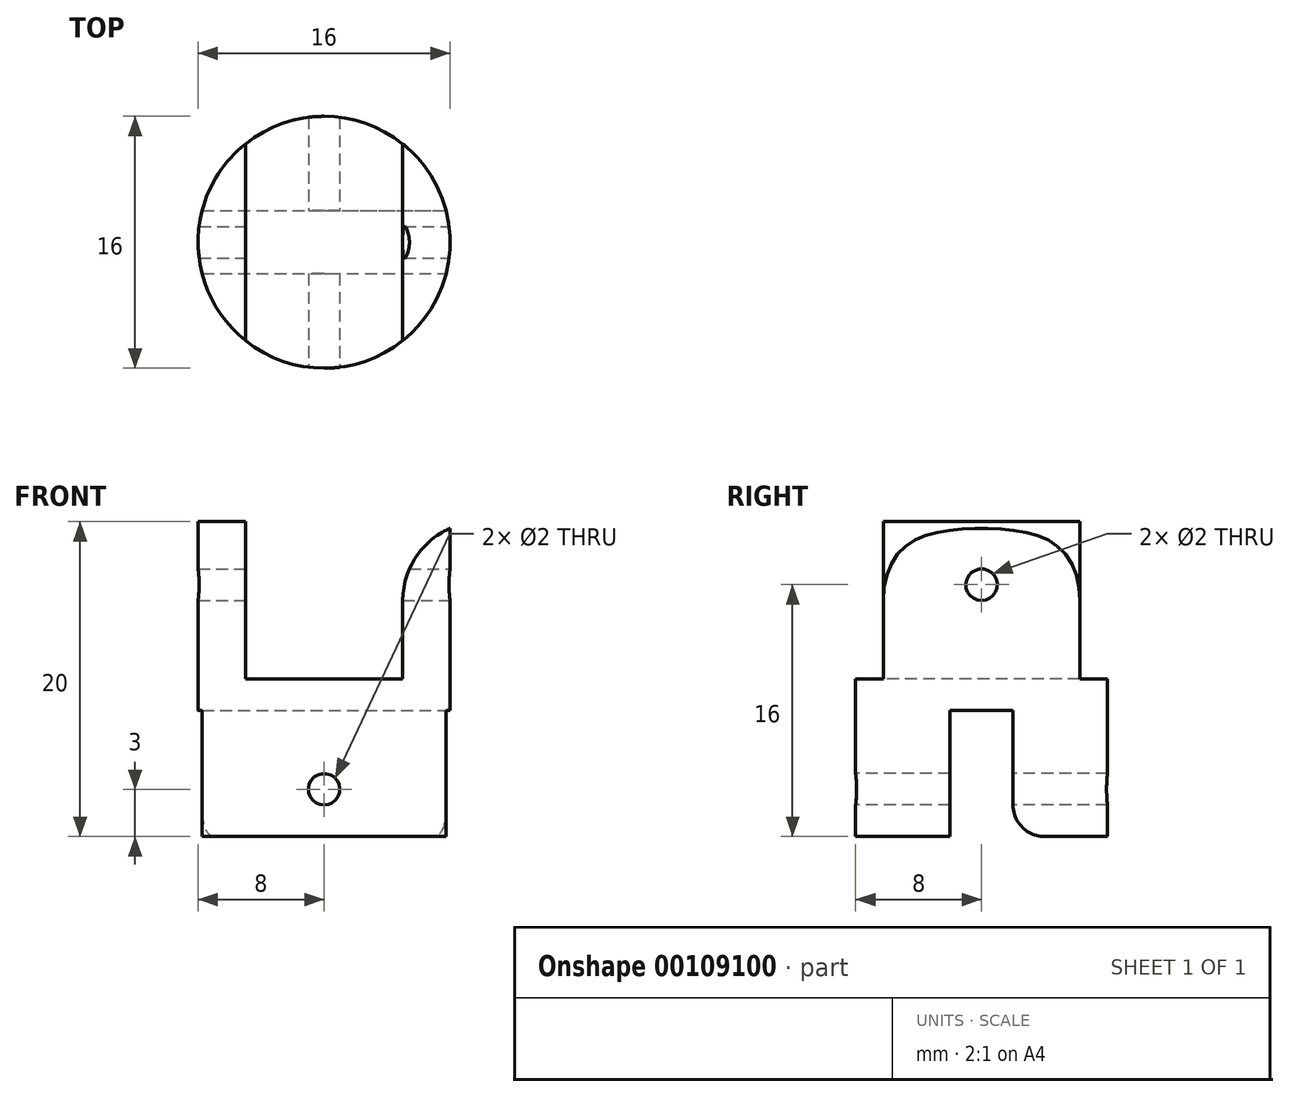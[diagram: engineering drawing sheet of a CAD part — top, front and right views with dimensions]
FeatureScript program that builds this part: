
annotation { "Feature Type Name" : "Feature", "Feature Type Description" : "" }
export const myFeature = defineFeature(function(context is Context, id is Id, definition is map)
    precondition{}
    {
        {
            var Q0;
            Q0=qCreatedBy(makeId("Top.planeOp"),FACE);
            var sketch = newSketch(context, id + "F0", { "sketchPlane" : qUnion([Q0])});
            skCircle(sketch, "E0", {"center": v(0, 0) * mm, "radius": 8 * mm});
            skSolve(sketch);
        }
        {
            var Q0;
            Q0 = qSketchRegion(id + "F0", true);
            extrude(context, id + "F1", {"entities" : qUnion([Q0]), "depth" : 20 * mm});
        }
        {
            var Q0;
            Q0=makeQuery(id+"F1.opExtrude","CAP_FACE",FACE,{"disambiguationData":[OSD([sQuery(id+"F0.wireOp",EDGE,"E0")])],"isStart":false});
            var sketch = newSketch(context, id + "F2", { "sketchPlane" : qUnion([Q0])});
            skLineSegment(sketch, "E1.bottom", {"start": v(-5, 8) * mm, "end": v(5, 8) * mm});
            skLineSegment(sketch, "E1.top", {"start": v(-5, -8) * mm, "end": v(5, -8) * mm});
            skLineSegment(sketch, "E1.left", {"start": v(-5, 8) * mm, "end": v(-5, -8) * mm});
            skLineSegment(sketch, "E1.right", {"start": v(5, 8) * mm, "end": v(5, -8) * mm});
            skPoint(sketch, "E1.middle", {"position": v(0, 0) * mm});
            skSolve(sketch);
        }
        {
            var Q0;
            Q0 = qSketchRegion(id + "F2", true);
            extrude(context, id + "F3", {"entities" : qUnion([Q0]), "operationType" : NewBodyOperationType.REMOVE, "oppositeDirection" : true, "depth" : 10 * mm});
        }
        {
            var Q0;
            Q0=makeQuery(id+"F1.opExtrude","CAP_FACE",FACE,{"disambiguationData":[OSD([sQuery(id+"F0.wireOp",EDGE,"E0")])],"isStart":true});
            var sketch = newSketch(context, id + "F4", { "sketchPlane" : qUnion([Q0])});
            skLineSegment(sketch, "E2.bottom", {"start": v(-8, -2) * mm, "end": v(8, -2) * mm});
            skLineSegment(sketch, "E2.top", {"start": v(-8, 2) * mm, "end": v(8, 2) * mm});
            skLineSegment(sketch, "E2.left", {"start": v(-8, -2) * mm, "end": v(-8, 2) * mm});
            skLineSegment(sketch, "E2.right", {"start": v(8, -2) * mm, "end": v(8, 2) * mm});
            skPoint(sketch, "E2.middle", {"position": v(0, 0) * mm});
            skSolve(sketch);
        }
        {
            var Q0;
            Q0 = qSketchRegion(id + "F4", true);
            extrude(context, id + "F5", {"entities" : qUnion([Q0]), "operationType" : NewBodyOperationType.REMOVE, "oppositeDirection" : true, "depth" : 8 * mm});
        }
        {
            var Q0;
            Q0=qCreatedBy(makeId("Right.planeOp"),FACE);
            var sketch = newSketch(context, id + "F6", { "sketchPlane" : qUnion([Q0])});
            skCircle(sketch, "E3", {"center": v(0, 16) * mm, "radius": 1 * mm});
            skSolve(sketch);
        }
        {
            var Q0;
            Q0 = qSketchRegion(id + "F6", true);
            extrude(context, id + "F7", {"entities" : qUnion([Q0]), "operationType" : NewBodyOperationType.REMOVE, "endBound" : BoundingType.SYMMETRIC, "oppositeDirection" : true, "depth" : 16 * mm});
        }
        {
            var Q0;
            Q0=qCreatedBy(makeId("Front.planeOp"),FACE);
            var sketch = newSketch(context, id + "F8", { "sketchPlane" : qUnion([Q0])});
            skCircle(sketch, "E4", {"center": v(0, 3) * mm, "radius": 1 * mm});
            skSolve(sketch);
        }
        {
            var Q0;
            Q0 = qSketchRegion(id + "F8", true);
            extrude(context, id + "F9", {"entities" : qUnion([Q0]), "operationType" : NewBodyOperationType.REMOVE, "endBound" : BoundingType.SYMMETRIC, "oppositeDirection" : true, "depth" : 16 * mm});
        }
        {
            var Q0;
            Q0=makeQuery(id+"F3.boolean.opBoolean","COPY",EDGE,{"derivedFrom":makeQuery(id+"F3.opExtrude","CAP_EDGE",EDGE,{"disambiguationData":[OSD([sQuery(id+"F2.wireOp",EDGE,"E1.left")])],"isStart":true})});
            var Q1;
            Q1=makeQuery(id+"F3.boolean.opBoolean","COPY",EDGE,{"derivedFrom":makeQuery(id+"F3.opExtrude","CAP_EDGE",EDGE,{"disambiguationData":[OSD([sQuery(id+"F2.wireOp",EDGE,"E1.right")])],"isStart":true})});
            fillet(context, id + "F10", {"entities" : qUnion([Q0, Q1]), "radius" : 5 * mm, "tangentPropagation" : true, "allowEdgeOverflow" : false});
        }
        {
            var Q0;
            Q0=makeQuery(id+"F5.boolean.opBoolean","COPY",EDGE,{"derivedFrom":makeQuery(id+"F5.opExtrude","CAP_EDGE",EDGE,{"disambiguationData":[OSD([sQuery(id+"F4.wireOp",EDGE,"E2.top")])],"isStart":true})});
            var Q1;
            Q1=makeQuery(id+"F5.boolean.opBoolean","COPY",EDGE,{"derivedFrom":makeQuery(id+"F5.opExtrude","CAP_EDGE",EDGE,{"disambiguationData":[OSD([sQuery(id+"F4.wireOp",EDGE,"E2.bottom")])],"isStart":true})});
            fillet(context, id + "F11", {"entities" : qUnion([Q0, Q1]), "radius" : 2 * mm, "tangentPropagation" : true, "allowEdgeOverflow" : false});
        }
    });
